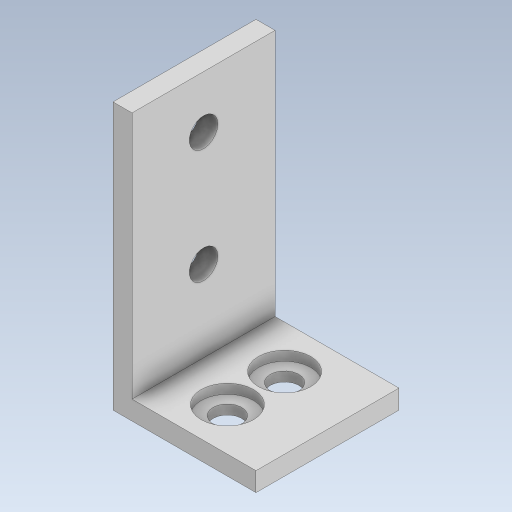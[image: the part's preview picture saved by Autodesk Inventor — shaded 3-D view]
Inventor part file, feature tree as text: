
AUTODESK INVENTOR PART (.ipt)
format: ipt  version: 2023.5 (Build 275446000, 446)  size: 141,312 bytes
history: native  units: in
note: dims shown in document units (in); Inventor stores cm internally (conversion verified against a paired STEP export)
features: extrude x4, sketch x2
ambient origin geometry x8: Origin, YZ Plane, XZ Plane, XY Plane, X Axis, Y Axis, Z Axis, Center Point
bodies: Solid1 (feature_tree)
feature tree (6):
  sketch  "Sketch1"  dims[d0=0.5906in d1=0.5906in]
  extrude  "Extrusion1"  Depth=0.5906in
  extrude  "Extrusion2"  Depth=0.1181in
  extrude  "Extrusion3"  Depth=0.0787in
  extrude  "Extrusion4"  Depth=0.0787in
  sketch  "Sketch2"  dims[d2=0.0787in d3=0.1181in d4=0.2165in d5=0.1772in d6=0.0787in d7=0.0in d8=0.0394in d9=0.0in d10=1.1024in d11=0.0in d12=0.1181in d13=0.3346in d14=0.1181in d15=0.8071in d16=0.0787in d17=0.0in]
